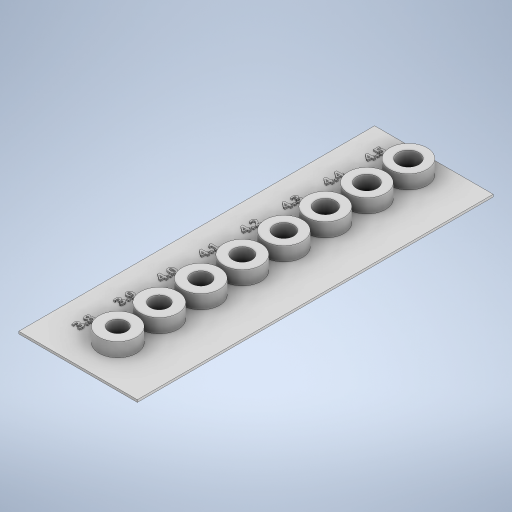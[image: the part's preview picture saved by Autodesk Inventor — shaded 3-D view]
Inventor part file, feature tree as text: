
AUTODESK INVENTOR PART (.ipt)
format: ipt  version: 2024.3 (Build 283343000, 343)  size: 778,752 bytes
history: native  units: in
note: dims shown in document units (in); Inventor stores cm internally (conversion verified against a paired STEP export)
features: projected_geometry x14, extrude x4, sketch x4
ambient origin geometry x8: Origin, YZ Plane, XZ Plane, XY Plane, X Axis, Y Axis, Z Axis, Center Point
bodies: Solid1 (feature_tree)
feature tree (22):
  extrude  "Extrusion1"  Depth=1.0in
  extrude  "Extrusion2"  Depth=0.0197in
  sketch  "Sketch3"  dims[d5=2.3622in d7=0.35in d8=0.3937in d10=1.0in d12=0.1181in d13=0.0in]
  extrude  "Extrusion3"  Depth=0.1181in TaperAngle=0.0deg
  extrude  "Extrusion4"  Depth=0.0118in
  sketch  "Sketch1"  dims[d0=3.0in d1=1.0in]
  sketch  "Sketch2"  dims[d2=0.0197in d3=0.0in d4=0.315in]
  projected_geometry  "Projected Loop1"
  projected_geometry  "Projected Loop2"
  projected_geometry  "Projected Loop3"
  projected_geometry  "Projected Loop4"
  projected_geometry  "Projected Loop5"
  projected_geometry  "Projected Loop6"
  projected_geometry  "Projected Loop7"
  projected_geometry  "Projected Loop8"
  sketch  "Sketch4"  dims[d14=0.1496in d15=0.1535in d16=0.1575in d17=0.1614in d18=0.1654in d19=0.1693in d20=1.1811in d22=0.35in d23=0.3937in d25=1.0in d27=0.1732in d28=0.1772in d30=0.1181in d31=0.0in d33=0.25in d34=3.1496in d36=0.35in d37=0.3937in d39=1.0in d41=0.0118in d42=0.0in]
  projected_geometry  "Projected Loop9"
  projected_geometry  "Projected Loop10"
  projected_geometry  "Projected Loop11"
  projected_geometry  "Projected Loop12"
  projected_geometry  "Projected Loop13"
  projected_geometry  "Projected Loop14"
